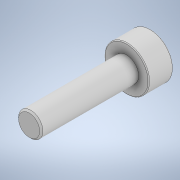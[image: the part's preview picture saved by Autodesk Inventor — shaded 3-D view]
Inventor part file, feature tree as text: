
AUTODESK INVENTOR PART (.ipt)
format: ipt  version: 2022 (Build 260153000, 153)  size: 136,704 bytes
history: native  units: in
note: dims shown in document units (in); Inventor stores cm internally (conversion verified against a paired STEP export)
features: sketch x3, extrude x2, fillet x1, chamfer x1
ambient origin geometry x8: Origin, YZ Plane, XZ Plane, XY Plane, X Axis, Y Axis, Z Axis, Center Point
bodies: Body1 (feature_tree)
feature tree (7):
  extrude  "Extrusion2"  Depth=0.4724in TaperAngle=0.0deg
  extrude  "Extrusion1"  Depth=0.0039in
  fillet  "Fillet1"  Radius=0.0039in
  chamfer  "Chamfer1"  Distance=0.0079in
  sketch  "Sketch1"  dims[d0=0.1181in d1=0.0in d2=0.4724in d3=0.0in]
  sketch  "Sketch2"  dims[d4=0.1181in d5=0.0in d6=0.0039in d7=0.0039in d8=0.0079in d9=0.0079in d10=17.7165in]
  sketch  "Sketch3"
